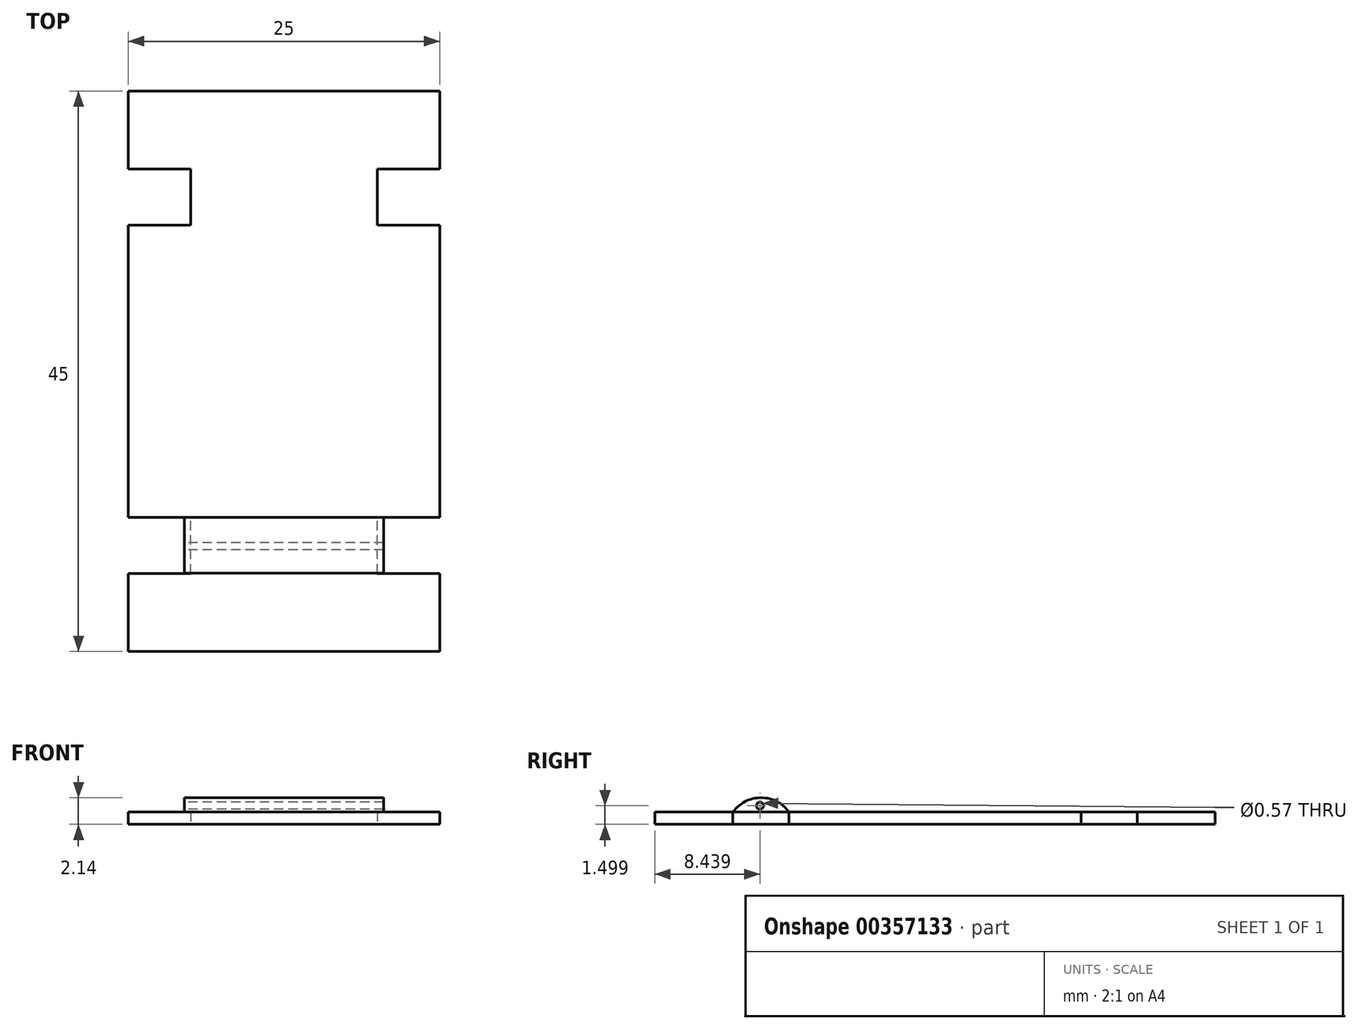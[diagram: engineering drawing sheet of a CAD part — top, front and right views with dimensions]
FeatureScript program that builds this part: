
annotation { "Feature Type Name" : "Feature", "Feature Type Description" : "" }
export const myFeature = defineFeature(function(context is Context, id is Id, definition is map)
    precondition{}
    {
        {
            var Q0;
            Q0=qCreatedBy(makeId("Top.planeOp"),FACE);
            var sketch = newSketch(context, id + "F0", { "sketchPlane" : qUnion([Q0])});
            skLineSegment(sketch, "E0.bottom", {"start": v(-12.5, -22.5) * mm, "end": v(12.5, -22.5) * mm});
            skLineSegment(sketch, "E0.top", {"start": v(-12.5, 22.5) * mm, "end": v(12.5, 22.5) * mm});
            skLineSegment(sketch, "E0.left", {"start": v(-12.5, -22.5) * mm, "end": v(-12.5, 22.5) * mm});
            skLineSegment(sketch, "E0.right", {"start": v(12.5, -22.5) * mm, "end": v(12.5, 22.5) * mm});
            skPoint(sketch, "E0.middle", {"position": v(0, 0) * mm});
            skLineSegment(sketch, "E1.bottom", {"start": v(-12.5, 16.23) * mm, "end": v(-7.5, 16.23) * mm});
            skLineSegment(sketch, "E1.top", {"start": v(-12.5, 11.73) * mm, "end": v(-7.5, 11.73) * mm});
            skLineSegment(sketch, "E1.left", {"start": v(-12.5, 16.23) * mm, "end": v(-12.5, 11.73) * mm});
            skLineSegment(sketch, "E1.right", {"start": v(-7.5, 16.23) * mm, "end": v(-7.5, 11.73) * mm});
            skLineSegment(sketch, "E2.MirrorCS", {"start": v(7.5, 16.23) * mm, "end": v(7.5, 11.73) * mm});
            skLineSegment(sketch, "E3.MirrorCS", {"start": v(12.5, 11.73) * mm, "end": v(7.5, 11.73) * mm});
            skLineSegment(sketch, "E4.MirrorCS", {"start": v(12.5, 16.23) * mm, "end": v(7.5, 16.23) * mm});
            skLineSegment(sketch, "E5.MirrorCS", {"start": v(-12.5, -11.73) * mm, "end": v(-7.5, -11.73) * mm});
            skLineSegment(sketch, "E6.MirrorCS", {"start": v(-7.5, -16.23) * mm, "end": v(-7.5, -11.73) * mm});
            skLineSegment(sketch, "E7.MirrorCS", {"start": v(-12.5, -16.23) * mm, "end": v(-7.5, -16.23) * mm});
            skLineSegment(sketch, "E8.MirrorCS", {"start": v(12.5, -11.73) * mm, "end": v(7.5, -11.73) * mm});
            skLineSegment(sketch, "E9.MirrorCS", {"start": v(7.5, -16.23) * mm, "end": v(7.5, -11.73) * mm});
            skLineSegment(sketch, "E10.MirrorCS", {"start": v(12.5, -16.23) * mm, "end": v(7.5, -16.23) * mm});
            skSolve(sketch);
        }
        {
            var Q0;
            {var subQ5=sQuery(id+"F0.wireOp",EDGE,"E0.bottom");Q0=makeQuery(id+"F0.imprint","IMPRINT",FACE,{"disambiguationData":[TD([[makeQuery(id+"F0.imprint","IMPRINT",EDGE,{"derivedFrom":subQ5}),1.0]])]});}
            extrude(context, id + "F1", {"entities" : qUnion([Q0]), "endBound" : BoundingType.SYMMETRIC, "depth" : 1 * mm});
        }
        {
            var Q0;
            Q0=qCreatedBy(makeId("Right.planeOp"),FACE);
            var sketch = newSketch(context, id + "F2", { "sketchPlane" : qUnion([Q0])});
            skArc(sketch, "E11", {"start": v(-11.73, 0.5) * mm, "mid": v(-13.98, 1.64) * mm, "end": v(-16.23, 0.5) * mm});
            skCircle(sketch, "E12", {"center": v(-14.06, 1) * mm, "radius": 0.28 * mm});
            skLineSegment(sketch, "E13", {"start": v(-16.23, 0.5) * mm, "end": v(-11.73, 0.5) * mm});
            skArc(sketch, "E14.MirrorCS", {"start": v(11.73, 0.5) * mm, "mid": v(13.98, 1.64) * mm, "end": v(16.23, 0.5) * mm});
            skLineSegment(sketch, "E15.MirrorCS", {"start": v(16.23, 0.5) * mm, "end": v(11.73, 0.5) * mm});
            skCircle(sketch, "E16.MirrorC", {"center": v(14.06, 1) * mm, "radius": 0.28 * mm});
            skSolve(sketch);
        }
        {
            var Q0;
            Q0=makeQuery(id+"F2.imprint","IMPRINT",FACE,{"disambiguationData":[TD([[makeQuery(id+"F2.imprint","IMPRINT",EDGE,{"derivedFrom":sQuery(id+"F2.wireOp",EDGE,"E11")}),1.0]])]});
            var Q1;
            Q1=makeQuery(id+"F2.imprint","IMPRINT",FACE,{"disambiguationData":[TD([[makeQuery(id+"F2.imprint","IMPRINT",EDGE,{"derivedFrom":sQuery(id+"F2.wireOp",EDGE,"E14.MirrorCS")}),-1.0]])]});
            extrude(context, id + "F3", {"entities" : qUnion([Q0, Q1]), "endBound" : BoundingType.SYMMETRIC, "depth" : 16 * mm});
        }
    });
